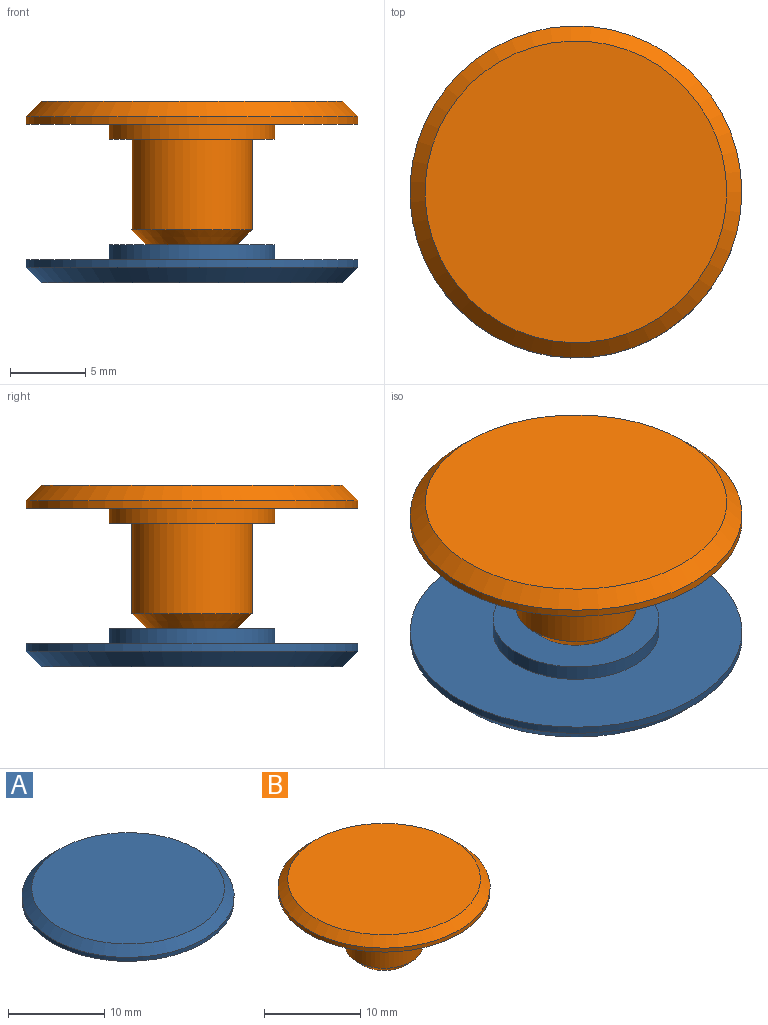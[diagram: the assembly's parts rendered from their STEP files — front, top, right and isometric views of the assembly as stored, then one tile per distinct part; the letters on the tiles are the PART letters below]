
ASSEMBLY  parts=2 mates=1
PART A: 9 faces, bbox 22x22x7.5 mm
  f0: cylinder r=1.95mm len=4mm, axis (0,0,-1), area 49mm2, adj f3,f7
  f1: plane 1.9x1.9mm, normal (0,0,-1), area 2.8mm2, adj f7
  f2: cylinder r=5.5mm len=11mm, axis (0,0,-1), area 34.6mm2, adj f3,f6
  f3: plane 11x11mm, normal (0,0,-1), area 83.1mm2, adj f0,f2
  f4: cylinder r=11mm len=22mm, axis (0,0,-1), area 34.6mm2, adj f6,f8
  f5: plane 20x20mm, normal (0,0,1), area 314.2mm2, adj f8
  f6: plane 22x22mm, normal (0,0,-1), area 285.1mm2, adj f2,f4
  f7: cone r=1.95mm half-angle=45deg, axis (0,0,1), area 12.9mm2, adj f0,f1
  f8: cone r=10mm half-angle=45deg, axis (0,0,-1), area 93.3mm2, adj f4,f5
PART B: 11 faces, bbox 22x22x9.5 mm
  f0: cylinder r=4mm len=8mm, axis (0,0,-1), area 150.8mm2, adj f3,f9
  f1: plane 6x6mm, normal (0,0,-1), area 15.7mm2, adj f7,f9
  f2: cylinder r=5.5mm len=11mm, axis (0,0,-1), area 34.6mm2, adj f3,f6
  f3: plane 11x11mm, normal (0,0,-1), area 44.8mm2, adj f0,f2
  f4: cylinder r=11mm len=22mm, axis (0,0,-1), area 34.6mm2, adj f6,f10
  f5: plane 20x20mm, normal (0,0,1), area 314.2mm2, adj f10
  f6: plane 22x22mm, normal (0,0,-1), area 285.1mm2, adj f2,f4
  f7: cylinder r=2mm len=5mm, axis (0,0,-1), area 62.8mm2, adj f1,f8
  f8: plane 4x4mm, normal (0,0,-1), area 12.6mm2, adj f7
  f9: cone r=4mm half-angle=45deg, axis (0,0,1), area 31.1mm2, adj f0,f1
  f10: cone r=10mm half-angle=45deg, axis (0,0,-1), area 93.3mm2, adj f4,f5
PLACE A rot(axis=(1,0,0),180deg) t=(-8.24,-34.22,-36.69)mm
PLACE B t=(-8.24,-34.22,-41.69)mm
MATE fastened A.f0 <-> B.f0  axis (0,0,1) through (-8.24,-34.22,-36.69)mm
